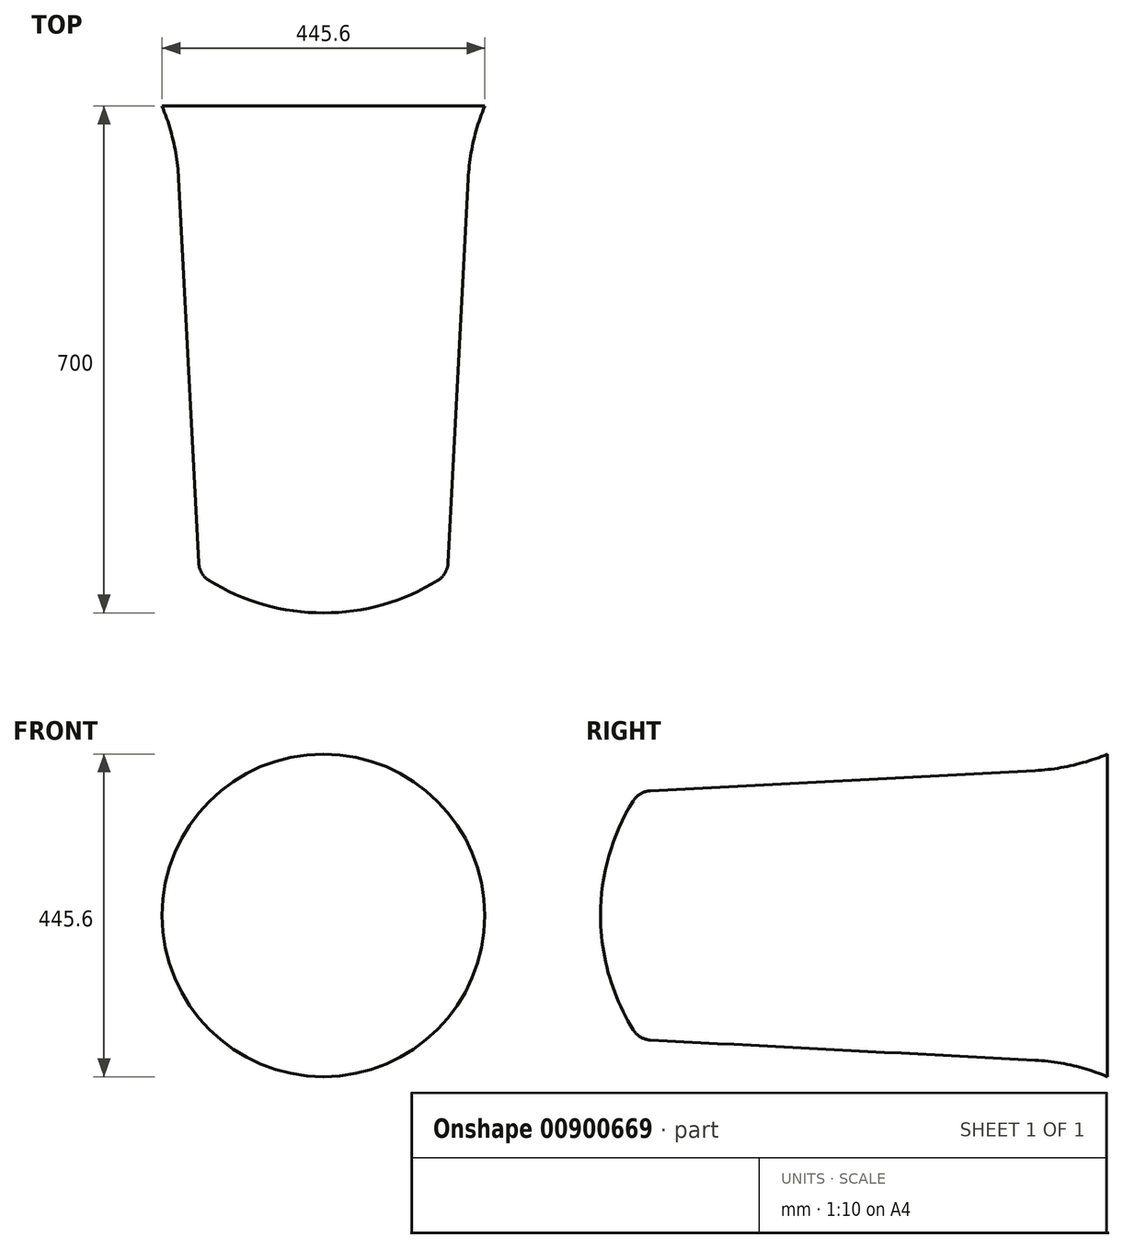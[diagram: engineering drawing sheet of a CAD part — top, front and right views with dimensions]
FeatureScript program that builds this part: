
annotation { "Feature Type Name" : "Feature", "Feature Type Description" : "" }
export const myFeature = defineFeature(function(context is Context, id is Id, definition is map)
    precondition{}
    {
        {
            var Q0;
            Q0=qCreatedBy(makeId("Right.planeOp"),FACE);
            var sketch = newSketch(context, id + "F0", { "sketchPlane" : qUnion([Q0])});
            skLineSegment(sketch, "E0", {"start": v(0, 0) * mm, "end": v(700, 0) * mm, "construction": true});
            skArc(sketch, "E1", {"start": v(0, 0) * mm, "mid": v(11.47, 82.14) * mm, "end": v(44.98, 158) * mm});
            skLineSegment(sketch, "E2", {"start": v(68.92, 172.17) * mm, "end": v(600, 200) * mm});
            skArc(sketch, "E3", {"start": v(600, 200) * mm, "mid": v(650.98, 207.1) * mm, "end": v(700, 222.8) * mm});
            skPoint(sketch, "E4.visualSharp", {"position": v(53.77, 171.37) * mm});
            skArc(sketch, "E4.filletArc", {"start": v(68.92, 172.17) * mm, "mid": v(55.21, 168.03) * mm, "end": v(44.98, 158) * mm});
            skSolve(sketch);
        }
        {
            var Q0;
            Q0=sQuery(id+"F0.wireOp",EDGE,"E3");
            var Q1;
            Q1=sQuery(id+"F0.wireOp",EDGE,"E2");
            var Q2;
            Q2=sQuery(id+"F0.wireOp",EDGE,"E4.filletArc");
            var Q3;
            Q3=sQuery(id+"F0.wireOp",EDGE,"E1");
            var Q4;
            Q4=sQuery(id+"F0.wireOp",EDGE,"E0");
            revolve(context, id + "F1", {"bodyType" : ToolBodyType.SURFACE, "surfaceOperationType" : NewSurfaceOperationType.NEW, "surfaceEntities" : qUnion([Q0, Q1, Q2, Q3]), "axis" : qUnion([Q4]), "revolveType" : RevolveType.ONE_DIRECTION, "oppositeDirection" : true, "angle" : 180 * degree});
        }
        {
            var Q0;
            Q0 = qSketchRegion(id + "F0", true);
            var Q1;
            Q1=makeQuery(id+"F1.opRevolve","CAP_EDGE",EDGE,{"disambiguationData":[OSD([sQuery(id+"F0.wireOp",EDGE,"E3")])],"isStart":true});
            var Q2;
            Q2=makeQuery(id+"F1.opRevolve","CAP_EDGE",EDGE,{"disambiguationData":[OSD([sQuery(id+"F0.wireOp",EDGE,"E2")])],"isStart":true});
            var Q3;
            Q3=sQuery(id+"F0.wireOp",EDGE,"E4.filletArc");
            var Q4;
            Q4=sQuery(id+"F0.wireOp",EDGE,"E1");
            var Q5;
            Q5=sQuery(id+"F0.wireOp",EDGE,"E0");
            revolve(context, id + "F2", {"bodyType" : ToolBodyType.SURFACE, "surfaceOperationType" : NewSurfaceOperationType.ADD, "entities" : qUnion([Q0]), "surfaceEntities" : qUnion([Q1, Q2, Q3, Q4]), "axis" : qUnion([Q5]), "revolveType" : RevolveType.ONE_DIRECTION, "angle" : 180 * degree});
        }
    });
